# Revit family: Sink_Floor_Industrial_12x12x8_Zurn-Z1851
name_source: partatom
category: Plumbing Fixtures
units: mm (PartAtom-declared; Revit-internal decimal feet)

## family parameters
Always vertical = Yes
Cut with Voids When Loaded = No
Maintain Annotation Orientation = No
OmniClass Number = 23.70.50.21.24.14
OmniClass Title = Deck Waste Water Drains
Part Type = Normal
Room Calculation Point = No
Round Connector Dimension = Use Radius
Shared = No
Work Plane-Based = No

## types (32) — shared parameters
Approx. Weight (Lbs) = 11 "
Assembly Code = D2030300
CW Connection = No
Default Elevation = 2 "
Description = 12” x 12”[305 x 305] SQUARE x 8” [203] DEEP INDUSTRIAL SANITARY FLOOR SINK
HW Connection = No
Manufacturer = Zurn Water, LLC
Manufacurer Brand = Zurn
Modified Date = 10/17/25
Product Documentation Link = https://files.zurn.com
Product Page URL = https://www.zurn.com
Product data url = https://www.bimobject.com
Sump Height = 8 "
URL = www.zurn.com
Vent Connection = No
WFU = 1
Waste Connection = Yes
zero-valued in all types: CWFU, HWFU

## per-type parameters (varying)
| type | 'E' Outlet HT Dim | Main Material | Model | Pipe Size 'A' (Inner Diameter) | Pipe Size 'A' (Inner Radius) | Pipe Size 'A' (Nominal Diameter) | Pipe Size 'A' (Nominal Radius) | Pipe Size 'A' (Outer Diameter) | Pipe Size 'A' (Outer Radius) | Type Comments |
| Z1851-2BW | 11 " | Steel - Zurn - Stainless - Type - 304 | Z1851 | 2.067 " | 1.034 " | 2 " | 1 " | 2.375 " | 1.188 " | Z1851 2 inch Butt-Weld Outlet |
| Z1851-3BW | 11 " | Steel - Zurn - Stainless - Type - 304 | Z1851 | 3.068 " | 1.534 " | 3 " | 1.5 " | 3.5 " | 1.75 " | Z1851 3 inch Butt-Weld Outlet |
| Z1851-4BW | 11 " | Steel - Zurn - Stainless - Type - 304 | Z1851 | 4.026 " | 2.013 " | 4 " | 2 " | 4.5 " | 2.25 " | Z1851 4 inch Butt-Weld Outlet |
| Z1851-6BW | 11 " | Steel - Zurn - Stainless - Type - 304 | Z1851 | 6.065 " | 3.033 " | 6 " | 3 " | 6.625 " | 3.313 " | Z1851 6 inch Butt-Weld Outlet |
| Z1851-2NH | 11 " | Steel - Zurn - Stainless - Type - 304 | Z1851 | 2.067 " | 1.034 " | 2 " | 1 " | 2.375 " | 1.188 " | Z1851 2 inch No-Hub Outlet |
| Z1851-3NH | 11 " | Steel - Zurn - Stainless - Type - 304 | Z1851 | 3.068 " | 1.534 " | 3 " | 1.5 " | 3.5 " | 1.75 " | Z1851 3 inch No-Hub Outlet |
| Z1851-4NH | 11 " | Steel - Zurn - Stainless - Type - 304 | Z1851 | 4.026 " | 2.013 " | 4 " | 2 " | 4.5 " | 2.25 " | Z1851 4 inch No-Hub Outlet |
| Z1851-6NH | 11 " | Steel - Zurn - Stainless - Type - 304 | Z1851 | 6.065 " | 3.033 " | 6 " | 3 " | 6.625 " | 3.313 " | Z1851 6 inch No-Hub Outlet |
| Z1851-2IP | 11 " | Steel - Zurn - Stainless - Type - 304 | Z1851 | 2.067 " | 1.034 " | 2 " | 1 " | 2.375 " | 1.188 " | Z1851 2 inch Threaded Outlet |
| Z1851-3IP | 11 " | Steel - Zurn - Stainless - Type - 304 | Z1851 | 3.068 " | 1.534 " | 3 " | 1.5 " | 3.5 " | 1.75 " | Z1851 3 inch Threaded Outlet |
| Z1851-4IP | 11 " | Steel - Zurn - Stainless - Type - 304 | Z1851 | 4.026 " | 2.013 " | 4 " | 2 " | 4.5 " | 2.25 " | Z1851 4 inch Threaded Outlet |
| Z1851-6IP | 11 " | Steel - Zurn - Stainless - Type - 304 | Z1851 | 6.065 " | 3.033 " | 6 " | 3 " | 6.625 " | 3.313 " | Z1851 6 inch Threaded Outlet |
| Z1851-2A | 9.25 " | Steel - Zurn - Stainless - Type - 304 | Z1851 | 2.067 " | 1.034 " | 2 " | 1 " | 2.375 " | 1.188 " | Z1851 2 inch Adjustable Threaded Outlet |
| Z1851-3A | 9.5 " | Steel - Zurn - Stainless - Type - 304 | Z1851 | 3.068 " | 1.534 " | 3 " | 1.5 " | 3.5 " | 1.75 " | Z1851 3 inch Adjustable Threaded Outlet |
| Z1851-4A | 9.5 " | Steel - Zurn - Stainless - Type - 304 | Z1851 | 4.026 " | 2.013 " | 4 " | 2 " | 4.5 " | 2.25 " | Z1851 4 inch Adjustable Threaded Outlet |
| Z1851-6A | 10.5 " | Steel - Zurn - Stainless - Type - 304 | Z1851 | 6.065 " | 3.033 " | 6 " | 3 " | 6.625 " | 3.313 " | Z1851 6 inch Adjustable Threaded Outlet |
| ZM1851-2BW | 11 " | Steel - Zurn - Stainless - Type - 316 | ZM1851 | 2.067 " | 1.034 " | 2 " | 1 " | 2.375 " | 1.188 " | ZM1851 2 inch Butt-Weld Outlet |
| ZM1851-3BW | 11 " | Steel - Zurn - Stainless - Type - 316 | ZM1851 | 3.068 " | 1.534 " | 3 " | 1.5 " | 3.5 " | 1.75 " | ZM1851 3 inch Butt-Weld Outlet |
| ZM1851-4BW | 11 " | Steel - Zurn - Stainless - Type - 316 | ZM1851 | 4.026 " | 2.013 " | 4 " | 2 " | 4.5 " | 2.25 " | ZM1851 4 inch Butt-Weld Outlet |
| ZM1851-6BW | 11 " | Steel - Zurn - Stainless - Type - 316 | ZM1851 | 6.065 " | 3.033 " | 6 " | 3 " | 6.625 " | 3.313 " | ZM1851 6 inch Butt-Weld Outlet |
| ZM1851-2NH | 11 " | Steel - Zurn - Stainless - Type - 316 | ZM1851 | 2.067 " | 1.034 " | 2 " | 1 " | 2.375 " | 1.188 " | ZM1851 2 inch No-Hub Outlet |
| ZM1851-3NH | 11 " | Steel - Zurn - Stainless - Type - 316 | ZM1851 | 3.068 " | 1.534 " | 3 " | 1.5 " | 3.5 " | 1.75 " | ZM1851 3 inch No-Hub Outlet |
| ZM1851-4NH | 11 " | Steel - Zurn - Stainless - Type - 316 | ZM1851 | 4.026 " | 2.013 " | 4 " | 2 " | 4.5 " | 2.25 " | ZM1851 4 inch No-Hub Outlet |
| ZM1851-6NH | 11 " | Steel - Zurn - Stainless - Type - 316 | ZM1851 | 6.065 " | 3.033 " | 6 " | 3 " | 6.625 " | 3.313 " | ZM1851 6 inch No-Hub Outlet |
| ZM1851-2IP | 11 " | Steel - Zurn - Stainless - Type - 316 | ZM1851 | 2.067 " | 1.034 " | 2 " | 1 " | 2.375 " | 1.188 " | ZM1851 2 inch Threaded Outlet |
| ZM1851-3IP | 11 " | Steel - Zurn - Stainless - Type - 316 | ZM1851 | 3.068 " | 1.534 " | 3 " | 1.5 " | 3.5 " | 1.75 " | ZM1851 3 inch Threaded Outlet |
| ZM1851-4IP | 11 " | Steel - Zurn - Stainless - Type - 316 | ZM1851 | 4.026 " | 2.013 " | 4 " | 2 " | 4.5 " | 2.25 " | ZM1851 4 inch Threaded Outlet |
| ZM1851-6IP | 11 " | Steel - Zurn - Stainless - Type - 316 | ZM1851 | 6.065 " | 3.033 " | 6 " | 3 " | 6.625 " | 3.313 " | ZM1851 6 inch Threaded Outlet |
| ZM1851-2A | 9.25 " | Steel - Zurn - Stainless - Type - 316 | ZM1851 | 2.067 " | 1.034 " | 2 " | 1 " | 2.375 " | 1.188 " | ZM1851 2 inch Adjustable Threaded Outlet |
| ZM1851-3A | 9.5 " | Steel - Zurn - Stainless - Type - 316 | ZM1851 | 3.068 " | 1.534 " | 3 " | 1.5 " | 3.5 " | 1.75 " | ZM1851 3 inch Adjustable Threaded Outlet |
| ZM1851-4A | 9.5 " | Steel - Zurn - Stainless - Type - 316 | ZM1851 | 4.026 " | 2.013 " | 4 " | 2 " | 4.5 " | 2.25 " | ZM1851 4 inch Adjustable Threaded Outlet |
| ZM1851-6A | 10.5 " | Steel - Zurn - Stainless - Type - 316 | ZM1851 | 6.065 " | 3.033 " | 6 " | 3 " | 6.625 " | 3.313 " | ZM1851 6 inch Adjustable Threaded Outlet |

## geometry (parser evidence)
native form markers: Sweep x5
no freeform markers — native parametric forms only
